# Revit family: Specialty_Equipment-Fiberstone_Planter-Stone_Yard-Barro-Round
name_source: partatom
category: Specialty Equipment
units: mm (PartAtom-declared; Revit-internal decimal feet)

## family parameters
Always vertical = Yes
Cut with Voids When Loaded = No
Enable Cutting in Views = No
Maintain Annotation Orientation = No
OmniClass Number = 23.40.05.21.17
OmniClass Title = Planters
Part Type = Normal
Room Calculation Point = No
Round Connector Dimension = Use Diameter
Shared = No
Work Plane-Based = No

## types (11) — shared parameters
Assembly Code = G2050600
CD_Finish = Concrete-Fiberstone-Carlsbad-Chalk
CD_Microsite = https://www.caddetails.com
CD_Product Page URL = https://stoneyardinc.com
CD_Specification = https://stoneyardinc.com
Default Elevation = 0.0"
Description = Barro Planter
Manufacturer = Stone Yard
Model = Barro Planter
Type Comments = Round Planter
URL = https://stoneyardinc.com

## per-type parameters (varying)
| type | CD_Diameter | CD_Fillet Height | CD_Height |
| 10"Dia x 12"H | 10.0" | 4.8" | 12.0" |
| 16"Dia x 18"H | 16.0" | 7.2" | 18.0" |
| 16"Dia x 20"H | 16.0" | 8.0" | 20.0" |
| 19"Dia x 28"H | 19.0" | 11.2" | 28.0" |
| 21"Dia x 21"H | 21.0" | 8.4" | 21.0" |
| 21"Dia x 24"H | 21.0" | 9.6" | 24.0" |
| 24"Dia x 29"H | 24.0" | 11.6" | 29.0" |
| 28"Dia x 44"H | 28.0" | 17.6" | 44.0" |
| 31.5"Dia x 24"H | 31.5" | 9.6" | 24.0" |
| 31.5"Dia x 35"H | 31.5" | 14.0" | 35.0" |
| 54"Dia x 34"H | 54.0" | 13.6" | 34.0" |

## geometry (parser evidence)
native form markers: Sweep x3
no freeform markers — native parametric forms only
